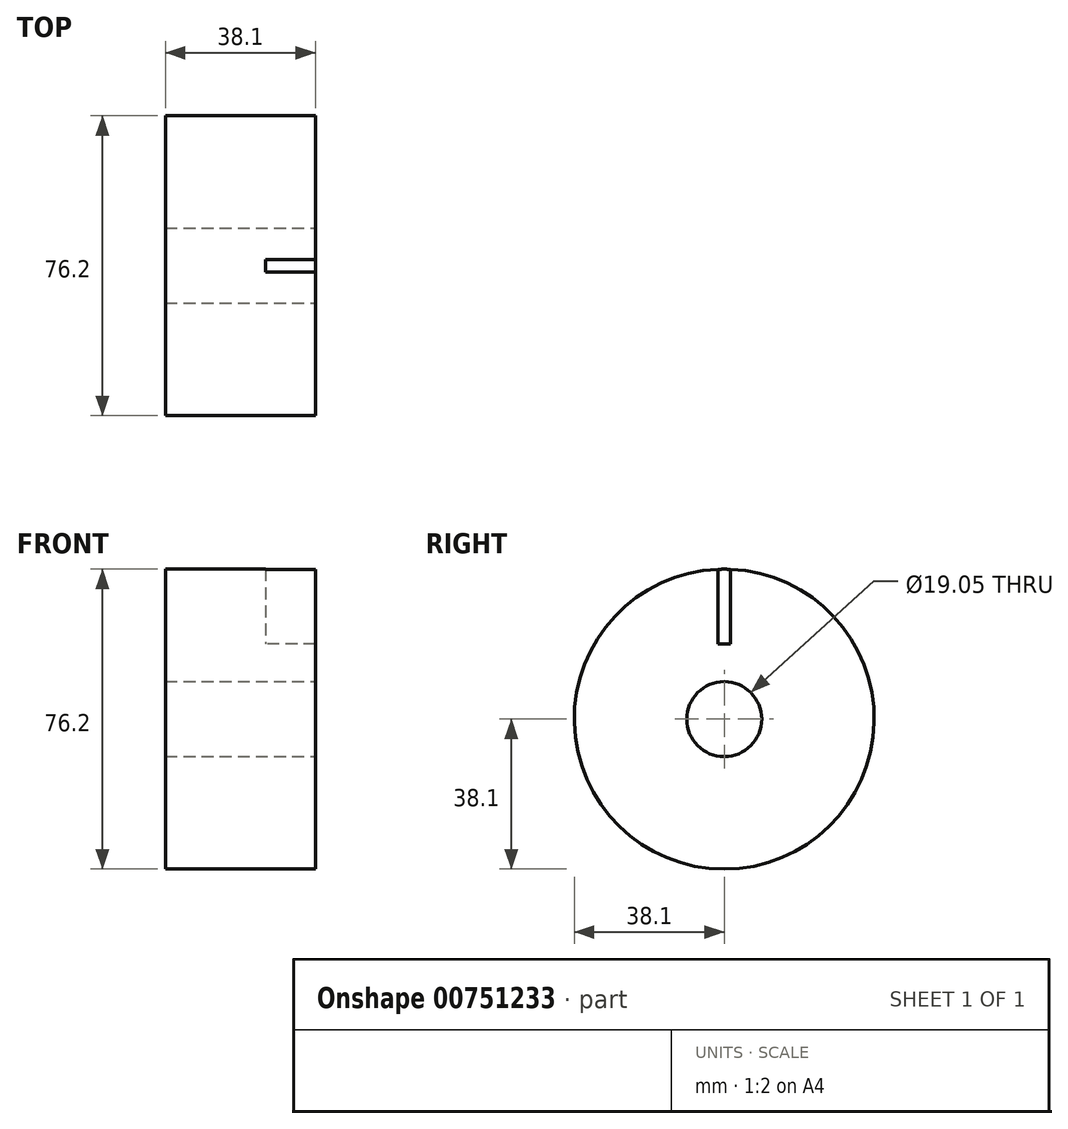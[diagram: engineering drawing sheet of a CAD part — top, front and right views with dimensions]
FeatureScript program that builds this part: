
annotation { "Feature Type Name" : "Feature", "Feature Type Description" : "" }
export const myFeature = defineFeature(function(context is Context, id is Id, definition is map)
    precondition{}
    {
        {
            var Q0;
            Q0=qCreatedBy(makeId("Right.planeOp"),FACE);
            var sketch = newSketch(context, id + "F0", { "sketchPlane" : qUnion([Q0])});
            skCircle(sketch, "E0", {"center": v(0, 0) * mm, "radius": 38.1 * mm});
            skSolve(sketch);
        }
        {
            var Q0;
            Q0 = qSketchRegion(id + "F0", true);
            extrude(context, id + "F1", {"entities" : qUnion([Q0]), "depth" : 38.1 * mm, "offsetDistance" : 25.4 * mm});
        }
        {
            var Q0;
            Q0=qCreatedBy(makeId("Top.planeOp"),FACE);
            var sketch = newSketch(context, id + "F2", { "sketchPlane" : qUnion([Q0])});
            skLineSegment(sketch, "E1.bottom", {"start": v(38.1, 1.59) * mm, "end": v(25.4, 1.59) * mm});
            skLineSegment(sketch, "E1.top", {"start": v(38.1, -1.59) * mm, "end": v(25.4, -1.59) * mm});
            skLineSegment(sketch, "E1.left", {"start": v(38.1, 1.59) * mm, "end": v(38.1, -1.59) * mm});
            skLineSegment(sketch, "E1.right", {"start": v(25.4, 1.59) * mm, "end": v(25.4, -1.59) * mm});
            skSolve(sketch);
        }
        {
            var Q0;
            Q0 = qSketchRegion(id + "F2", true);
            extrude(context, id + "F3", {"entities" : qUnion([Q0]), "operationType" : NewBodyOperationType.REMOVE, "depth" : 38.1 * mm, "offsetDistance" : 25.4 * mm, "hasSecondDirection" : true, "secondDirectionOppositeDirection" : false, "secondDirectionDepth" : 19.05 * mm});
        }
        {
            var Q0;
            Q0=makeQuery(id+"F1.opExtrude","CAP_FACE",FACE,{"disambiguationData":[OSD([sQuery(id+"F0.wireOp",EDGE,"E0")])],"isStart":false});
            var sketch = newSketch(context, id + "F4", { "sketchPlane" : qUnion([Q0])});
            skCircle(sketch, "E2", {"center": v(0, 0) * mm, "radius": 9.52 * mm});
            skSolve(sketch);
        }
        {
            var Q0;
            Q0 = qSketchRegion(id + "F4", true);
            extrude(context, id + "F5", {"entities" : qUnion([Q0]), "operationType" : NewBodyOperationType.REMOVE, "endBound" : BoundingType.THROUGH_ALL, "oppositeDirection" : true, "depth" : 25.4 * mm, "offsetDistance" : 25.4 * mm});
        }
    });
